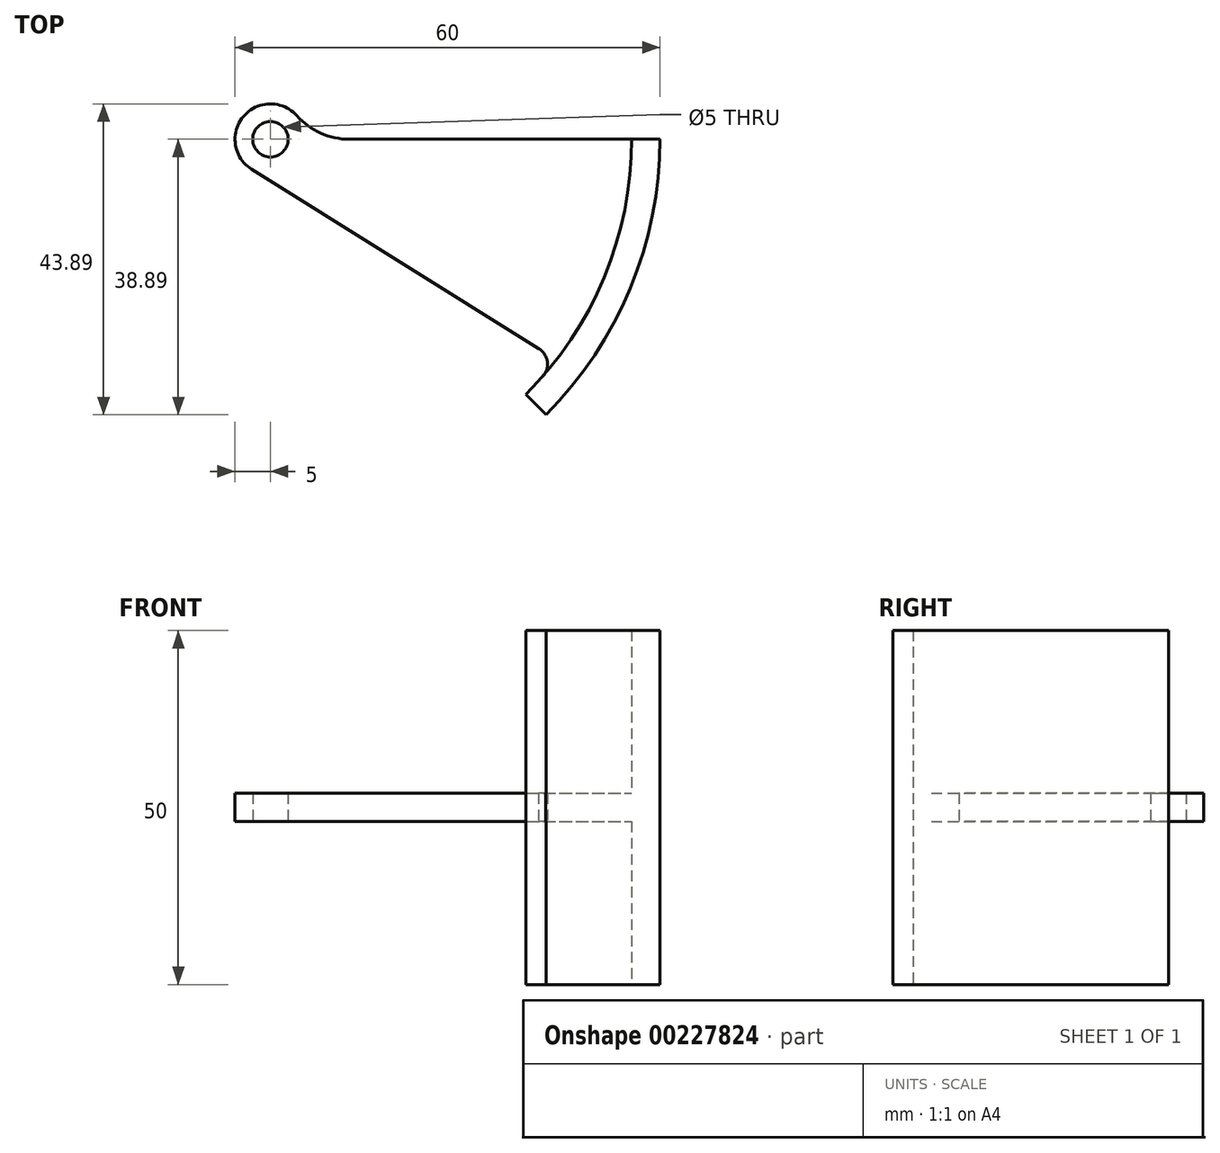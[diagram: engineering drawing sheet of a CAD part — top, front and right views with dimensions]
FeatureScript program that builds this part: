
annotation { "Feature Type Name" : "Feature", "Feature Type Description" : "" }
export const myFeature = defineFeature(function(context is Context, id is Id, definition is map)
    precondition{}
    {
        {
            var Q0;
            Q0=qCreatedBy(makeId("Top.planeOp"),FACE);
            var sketch = newSketch(context, id + "F0", { "sketchPlane" : qUnion([Q0])});
            skCircle(sketch, "E0", {"center": v(0, 0) * mm, "radius": 2.5 * mm});
            skArc(sketch, "E1", {"start": v(3.73, 3.33) * mm, "mid": v(-3.82, 3.22) * mm, "end": v(-2.65, -4.24) * mm});
            skLineSegment(sketch, "E2", {"start": v(-13.18, 5) * mm, "end": v(38.9, 5) * mm, "construction": true});
            skArc(sketch, "E3", {"start": v(38.89, -38.89) * mm, "mid": v(50.81, -21.05) * mm, "end": v(55, 0) * mm});
            skArc(sketch, "E4", {"start": v(3.73, 3.33) * mm, "mid": v(7.1, 0.87) * mm, "end": v(11.18, 0) * mm});
            skLineSegment(sketch, "E5.trimOffspring", {"start": v(11.18, 0) * mm, "end": v(55, 0) * mm});
            skPoint(sketch, "E6", {"position": v(55, 0) * mm});
            skArc(sketch, "E7", {"start": v(36.06, -36.06) * mm, "mid": v(37.3, -34.78) * mm, "end": v(38.5, -33.46) * mm});
            skLineSegment(sketch, "E8", {"start": v(-2.65, -4.24) * mm, "end": v(37.85, -29.55) * mm});
            skLineSegment(sketch, "E9", {"start": v(26.3, -25.87) * mm, "end": v(45.8, -38.05) * mm, "construction": true});
            skPoint(sketch, "E10", {"position": v(40.4, -31.14) * mm});
            skCircle(sketch, "E11", {"center": v(40.4, -31.14) * mm, "radius": 3 * mm, "construction": true});
            skPoint(sketch, "E12", {"position": v(37.85, -29.55) * mm});
            skArc(sketch, "E13.trimOffspring", {"start": v(40.4, -31.14) * mm, "mid": v(48.28, -16.45) * mm, "end": v(51, 0) * mm, "construction": true});
            skLineSegment(sketch, "E14.trimOffspring", {"start": v(40.4, -31.14) * mm, "end": v(64.64, -46.29) * mm});
            skArc(sketch, "E15", {"start": v(38.5, -33.46) * mm, "mid": v(39.09, -31.35) * mm, "end": v(37.85, -29.55) * mm});
            skLineSegment(sketch, "E16", {"start": v(0, 0) * mm, "end": v(15.72, -15.72) * mm});
            skLineSegment(sketch, "E17.trimOffspring", {"start": v(36.06, -36.06) * mm, "end": v(38.89, -38.89) * mm});
            skPoint(sketch, "E18", {"position": v(36.06, -36.06) * mm});
            skPoint(sketch, "E19", {"position": v(38.89, -38.89) * mm});
            skSolve(sketch);
        }
        {
            var Q0;
            Q0=qCreatedBy(makeId("Top.planeOp"),FACE);
            var sketch = newSketch(context, id + "F1", { "sketchPlane" : qUnion([Q0])});
            skArc(sketch, "E20", {"start": v(38.9, -38.9) * mm, "mid": v(50.81, -21.05) * mm, "end": v(55, 0) * mm});
            skArc(sketch, "E21", {"start": v(36.06, -36.06) * mm, "mid": v(47.12, -19.52) * mm, "end": v(51, 0) * mm});
            skLineSegment(sketch, "E22", {"start": v(51, 0) * mm, "end": v(55, 0) * mm});
            skLineSegment(sketch, "E23", {"start": v(55, 0) * mm, "end": v(51, 0) * mm});
            skLineSegment(sketch, "E24", {"start": v(36.06, -36.06) * mm, "end": v(38.9, -38.9) * mm});
            skSolve(sketch);
        }
        {
            var Q0;
            Q0 = qSketchRegion(id + "F0", true);
            extrude(context, id + "F2", {"entities" : qUnion([Q0]), "depth" : 2 * mm, "hasSecondDirection" : true, "secondDirectionOppositeDirection" : true, "secondDirectionDepth" : 2 * mm});
        }
        {
            var Q0;
            Q0 = qSketchRegion(id + "F1", true);
            extrude(context, id + "F3", {"entities" : qUnion([Q0]), "operationType" : NewBodyOperationType.ADD, "depth" : 25 * mm, "hasSecondDirection" : true, "secondDirectionOppositeDirection" : true, "secondDirectionDepth" : 25 * mm});
        }
    });
